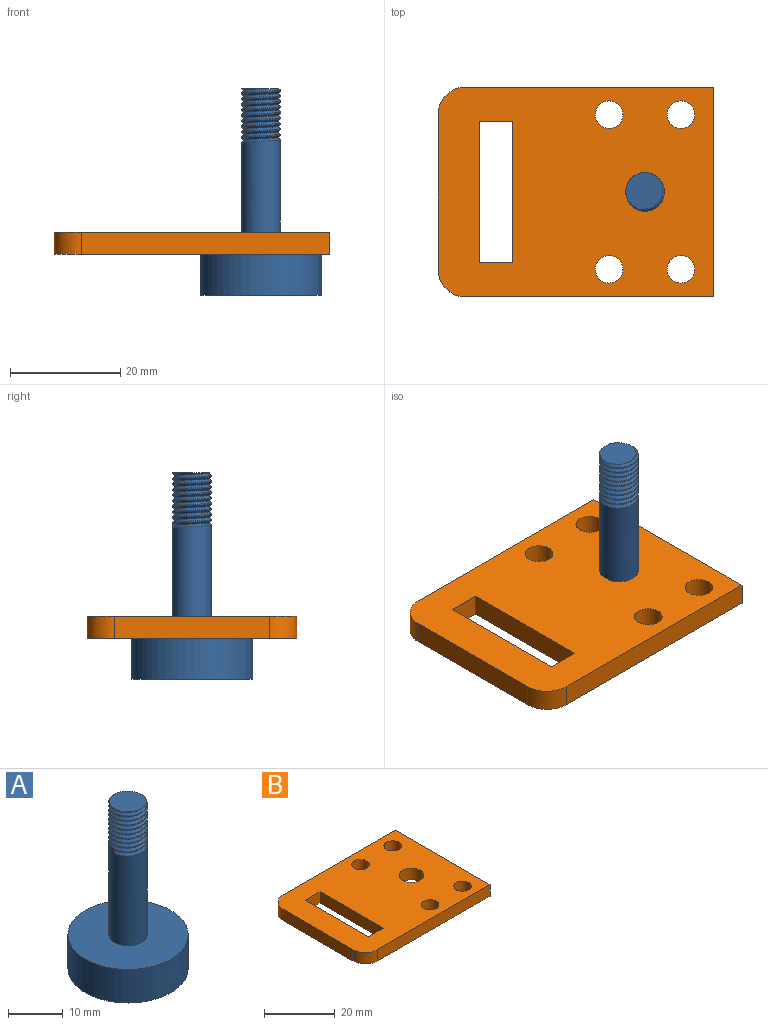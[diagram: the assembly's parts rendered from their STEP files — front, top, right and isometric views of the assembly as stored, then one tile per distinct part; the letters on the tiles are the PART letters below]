
ASSEMBLY  parts=2 mates=1
PART A: 18 faces, bbox 22.3x22.3x38.3 mm
  f0: cylinder r=3.5mm len=21mm, axis (0,0,-1), area 450.8mm2, adj f1,f13,f15,f17
  f1: cylinder r=3.5mm len=7mm, axis (0,0,-1), area 4.4mm2, adj f0,f2,f16,f17
  f2: cylinder r=3.5mm len=7mm, axis (0,0,-1), area 4.4mm2, adj f1,f3,f16,f17
  f3: cylinder r=3.5mm len=7mm, axis (0,0,-1), area 4.4mm2, adj f2,f4,f16,f17
  f4: cylinder r=3.5mm len=7mm, axis (0,0,-1), area 4.4mm2, adj f3,f5,f16,f17
  f5: cylinder r=3.5mm len=7mm, axis (0,0,-1), area 4.4mm2, adj f4,f6,f16,f17
  f6: cylinder r=3.5mm len=7mm, axis (0,0,-1), area 4.4mm2, adj f5,f7,f16,f17
  f7: cylinder r=3.5mm len=7mm, axis (0,0,-1), area 4.4mm2, adj f6,f8,f16,f17
  f8: cylinder r=3.5mm len=7mm, axis (0,0,-1), area 4.4mm2, adj f7,f9,f16,f17
  f9: cylinder r=3.5mm len=7mm, axis (0,0,-1), area 4.4mm2, adj f8,f10,f16,f17
  f10: cylinder r=3.5mm len=3.34mm, axis (0,0,-1), area 0.4mm2, adj f9,f14,f16
  f11: cylinder r=11mm len=22mm, axis (0,0,1), area 518.4mm2, adj f12,f13
  f12: plane 22x22mm, normal (0,0,-1), area 380.1mm2, adj f11
  f13: plane 22x22mm, normal (0,0,1), area 341.6mm2, adj f0,f11
  f14: plane 6.98x6.97mm, normal (0,0,1), area 35.1mm2, adj f10,f16,f17
  f15: plane 0.8x0.4mm, normal (0,-1,0), area 0.2mm2, adj f0,f16,f17
  f16: bspline ~10.07x8.08mm, area 110.3mm2, adj f1,f2,f3,f4,f5,f6,f7,f8
  f17: bspline ~10.57x8.08mm, area 115.1mm2, adj f0,f1,f2,f3,f4,f5,f6,f7
PART B: 17 faces, bbox 50x38x4 mm
  f0: plane 25.4x4mm, normal (-1,0,0), area 101.6mm2, adj f1,f6,f13,f14
  f1: plane 6x4mm, normal (0,1,0), area 24mm2, adj f0,f2,f13,f14
  f2: plane 25.4x4mm, normal (1,0,0), area 101.6mm2, adj f1,f6,f13,f14
  f3: plane 38x4mm, normal (1,0,0), area 152mm2, adj f4,f7,f13,f14
  f4: plane 45x4mm, normal (0,1,0), area 180mm2, adj f3,f13,f14,f15
  f5: plane 28x4mm, normal (-1,0,0), area 112mm2, adj f13,f14,f15,f16
  f6: plane 6x4mm, normal (0,-1,0), area 24mm2, adj f0,f2,f13,f14
  f7: plane 45x4mm, normal (0,-1,0), area 180mm2, adj f3,f13,f14,f16
  f8: cylinder r=2.5mm len=5mm, axis (0,0,-1), area 62.8mm2, adj f13,f14
  f9: cylinder r=2.5mm len=5mm, axis (0,0,-1), area 62.8mm2, adj f13,f14
  f10: cylinder r=2.5mm len=5mm, axis (0,0,-1), area 62.8mm2, adj f13,f14
  f11: cylinder r=3.5mm len=7mm, axis (0,0,-1), area 88mm2, adj f13,f14
  f12: cylinder r=2.5mm len=5mm, axis (0,0,-1), area 62.8mm2, adj f13,f14
  f13: plane 50x38mm, normal (0,0,1), area 1619.8mm2, adj f0,f1,f2,f3,f4,f5,f6,f7
  f14: plane 50x38mm, normal (0,0,-1), area 1619.8mm2, adj f0,f1,f2,f3,f4,f5,f6,f7
  f15: cylinder r=5mm len=5mm, axis (0,0,1), area 31.4mm2, adj f4,f5,f13,f14
  f16: cylinder r=5mm len=5mm, axis (0,0,-1), area 31.4mm2, adj f5,f7,f13,f14
PLACE A rot(axis=(0,0,-1),79.6deg) t=(-2.03,11.82,2.85)mm
PLACE B t=(-12.28,-0.47,2.85)mm fixed
MATE revolute A.f11 <-> B.f11  axis (0,0,1) through (0.22,-0.47,2.85)mm
